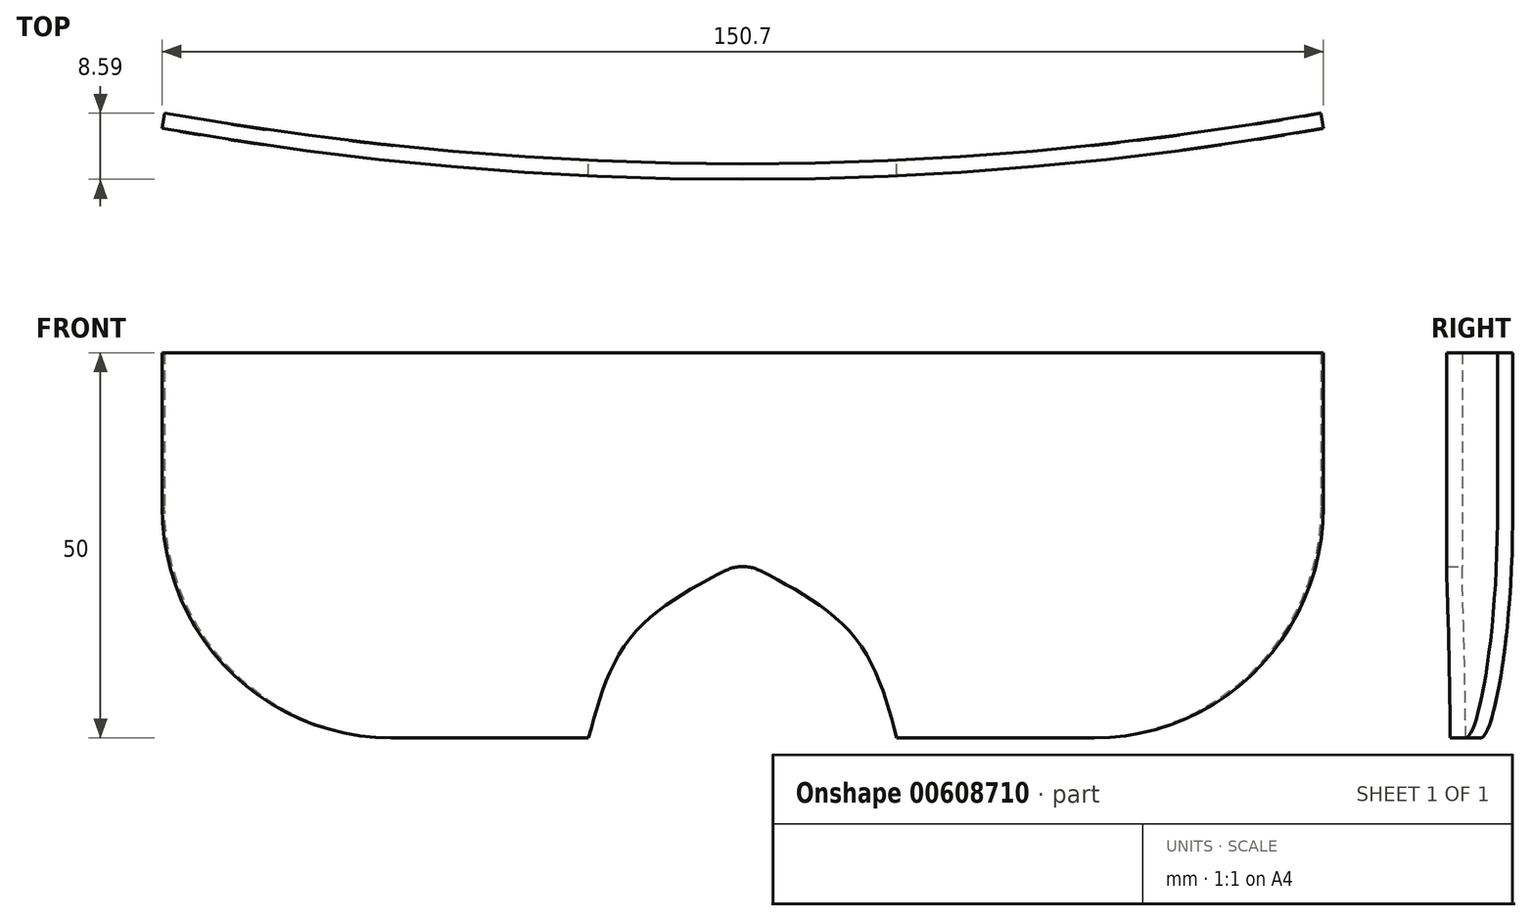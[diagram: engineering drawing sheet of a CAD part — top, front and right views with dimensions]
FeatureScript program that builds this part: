
annotation { "Feature Type Name" : "Feature", "Feature Type Description" : "" }
export const myFeature = defineFeature(function(context is Context, id is Id, definition is map)
    precondition{}
    {
        {
            var Q0;
            Q0=qCreatedBy(makeId("Top.planeOp"),FACE);
            var sketch = newSketch(context, id + "F0", { "sketchPlane" : qUnion([Q0])});
            skArc(sketch, "E0", {"start": v(-75, 0) * mm, "mid": v(0, -6.59) * mm, "end": v(75, 0) * mm});
            skArc(sketch, "E1.0", {"start": v(-75.35, -1.97) * mm, "mid": v(0, -8.59) * mm, "end": v(75.35, -1.97) * mm});
            skLineSegment(sketch, "E2", {"start": v(-75, 0) * mm, "end": v(-75.35, -1.97) * mm});
            skLineSegment(sketch, "E3", {"start": v(75, 0) * mm, "end": v(75.35, -1.97) * mm});
            skSolve(sketch);
        }
        {
            var Q0;
            Q0=makeQuery(id+"F0.imprint","IMPRINT",FACE,{"disambiguationData":[TD([[makeQuery(id+"F0.imprint","IMPRINT",EDGE,{"derivedFrom":sQuery(id+"F0.wireOp",EDGE,"E0")}),-1.0]])]});
            extrude(context, id + "F1", {"entities" : qUnion([Q0]), "depth" : 50 * mm, "offsetDistance" : 25 * mm});
        }
        {
            var Q0;
            Q0=makeQuery(id+"F1.opExtrude","CAP_EDGE",EDGE,{"disambiguationData":[OSD([sQuery(id+"F0.wireOp",EDGE,"E3")])],"isStart":true});
            var Q1;
            Q1=makeQuery(id+"F1.opExtrude","CAP_EDGE",EDGE,{"disambiguationData":[OSD([sQuery(id+"F0.wireOp",EDGE,"E2")])],"isStart":true});
            fillet(context, id + "F2", {"entities" : qUnion([Q0, Q1]), "radius" : 30 * mm, "tangentPropagation" : true, "allowEdgeOverflow" : false});
        }
        {
            var Q0;
            Q0=qCreatedBy(makeId("Front.planeOp"),FACE);
            var sketch = newSketch(context, id + "F3", { "sketchPlane" : qUnion([Q0])});
            skLineSegment(sketch, "E4", {"start": v(0, 0) * mm, "end": v(20, 0) * mm});
            skFitSpline(sketch, "E5", {"points": [v(20, 0) * mm, v(14.33, 13.3) * mm, v(0, 22.85) * mm], "startDerivative": vector(-8.14, 30.08) * mm, "endDerivative": vector(-31.52, 15.82) * mm});
            skFitSpline(sketch, "E6.MirrorCS", {"points": [v(-20, 0) * mm, v(-14.33, 13.3) * mm, v(0, 22.85) * mm], "startDerivative": vector(8.14, 30.08) * mm, "endDerivative": vector(31.52, 15.82) * mm});
            skLineSegment(sketch, "E7", {"start": v(20, 0) * mm, "end": v(-20, 0) * mm});
            skSolve(sketch);
        }
        {
            var Q0;
            {var subQ0=sQuery(id+"F3.wireOp",EDGE,"E5");Q0=makeQuery(id+"F3.imprint","IMPRINT",FACE,{"disambiguationData":[TD([[makeQuery(id+"F3.imprint","IMPRINT",EDGE,{"derivedFrom":subQ0}),1.0]])]});}
            var Q1;
            Q1=makeQuery(id+"F1.opExtrude","SWEPT_FACE",FACE,{"disambiguationData":[OSD([sQuery(id+"F0.wireOp",EDGE,"E1.0")])]});
            extrude(context, id + "F4", {"entities" : qUnion([Q0]), "operationType" : NewBodyOperationType.REMOVE, "endBound" : BoundingType.UP_TO_SURFACE, "depth" : 25 * mm, "endBoundEntityFace" : qUnion([Q1]), "offsetDistance" : 25 * mm});
        }
        {
            var Q0;
            Q0=makeQuery(id+"F4.boolean.opBoolean","COPY",EDGE,{"derivedFrom":makeQuery(id+"F4.opExtrude","SWEPT_EDGE",EDGE,{"disambiguationData":[OSD([sQuery(id+"F3.wireOp",EDGE,"E5"),sQuery(id+"F3.wireOp",EDGE,"E6.MirrorCS")])]})});
            fillet(context, id + "F5", {"entities" : qUnion([Q0]), "radius" : 5 * mm, "tangentPropagation" : true, "allowEdgeOverflow" : false});
        }
    });
